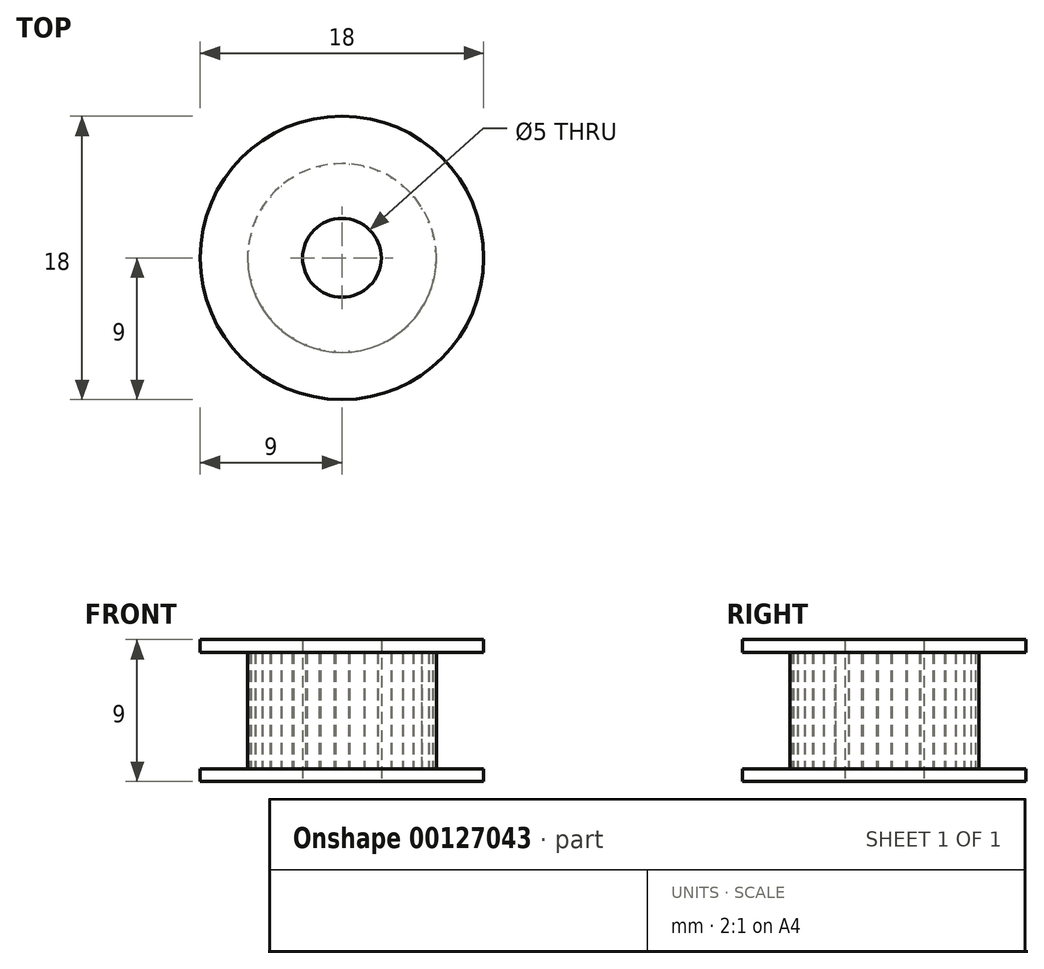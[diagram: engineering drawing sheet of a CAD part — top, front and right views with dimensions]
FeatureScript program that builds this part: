
annotation { "Feature Type Name" : "Feature", "Feature Type Description" : "" }
export const myFeature = defineFeature(function(context is Context, id is Id, definition is map)
    precondition{}
    {
        {
            var Q0;
            Q0=qCreatedBy(makeId("Top.planeOp"),FACE);
            var sketch = newSketch(context, id + "F0", { "sketchPlane" : qUnion([Q0])});
            skLineSegment(sketch, "E0", {"start": v(-19.17, 17.78) * mm, "end": v(-18.17, 17.78) * mm});
            skLineSegment(sketch, "E1", {"start": v(-18.17, 17.78) * mm, "end": v(-18.17, 18.4) * mm});
            skArc(sketch, "E2", {"start": v(-18.67, 18.85) * mm, "mid": v(-18.88, 19.07) * mm, "end": v(-19.17, 19.16) * mm});
            skArc(sketch, "E3", {"start": v(-18.58, 18.54) * mm, "mid": v(-18.61, 18.7) * mm, "end": v(-18.67, 18.85) * mm});
            skArc(sketch, "E4", {"start": v(-18.58, 18.54) * mm, "mid": v(-18.53, 18.44) * mm, "end": v(-18.43, 18.4) * mm});
            skLineSegment(sketch, "E5", {"start": v(-18.43, 18.4) * mm, "end": v(-18.17, 18.4) * mm});
            skArc(sketch, "E6.0.MirrorCS", {"start": v(-19.67, 18.85) * mm, "mid": v(-19.47, 19.07) * mm, "end": v(-19.17, 19.16) * mm});
            skArc(sketch, "E7.0.MirrorCS", {"start": v(-19.76, 18.54) * mm, "mid": v(-19.73, 18.7) * mm, "end": v(-19.67, 18.85) * mm});
            skArc(sketch, "E8.0.MirrorCS", {"start": v(-19.76, 18.54) * mm, "mid": v(-19.81, 18.44) * mm, "end": v(-19.91, 18.4) * mm});
            skLineSegment(sketch, "E9.0.MirrorCS", {"start": v(-19.91, 18.4) * mm, "end": v(-20.17, 18.4) * mm});
            skLineSegment(sketch, "E10.0.MirrorCS", {"start": v(-20.17, 17.78) * mm, "end": v(-20.17, 18.4) * mm});
            skLineSegment(sketch, "E11.0.MirrorCS", {"start": v(-19.17, 17.78) * mm, "end": v(-20.17, 17.78) * mm});
            skLineSegment(sketch, "E12.direction1", {"start": v(-20.17, 17.78) * mm, "end": v(-18.17, 17.78) * mm, "construction": true});
            skLineSegment(sketch, "E13", {"start": v(-20.17, 18.15) * mm, "end": v(-18.17, 18.15) * mm, "construction": true});
            skPoint(sketch, "E14", {"position": v(0, -5.25) * mm});
            skArc(sketch, "E15", {"start": v(0.38, -5.76) * mm, "mid": v(0, -5.25) * mm, "end": v(-0.38, -5.76) * mm});
            skArc(sketch, "E16", {"start": v(-0.38, -5.76) * mm, "mid": v(-0.38, -5.76) * mm, "end": v(-0.38, -5.77) * mm});
            skArc(sketch, "E17", {"start": v(0.38, -5.77) * mm, "mid": v(0.38, -5.76) * mm, "end": v(0.38, -5.76) * mm});
            skArc(sketch, "E18", {"start": v(0.4, -5.94) * mm, "mid": v(0.93, -5.88) * mm, "end": v(1.45, -5.77) * mm});
            skArc(sketch, "E19", {"start": v(0.38, -5.77) * mm, "mid": v(0.36, -5.9) * mm, "end": v(0.5, -5.93) * mm});
            skArc(sketch, "E20", {"start": v(-0.38, -5.77) * mm, "mid": v(-0.36, -5.9) * mm, "end": v(-0.5, -5.93) * mm});
            skArc(sketch, "E21.1.0", {"start": v(2.14, -5.36) * mm, "mid": v(1.62, -5) * mm, "end": v(1.42, -5.6) * mm});
            skPoint(sketch, "E21.1.1", {"position": v(1.62, -5) * mm});
            skArc(sketch, "E21.1.2", {"start": v(1.42, -5.6) * mm, "mid": v(1.42, -5.6) * mm, "end": v(1.42, -5.6) * mm});
            skArc(sketch, "E21.1.3", {"start": v(2.14, -5.37) * mm, "mid": v(2.17, -5.5) * mm, "end": v(2.3, -5.49) * mm});
            skArc(sketch, "E21.1.4", {"start": v(1.42, -5.6) * mm, "mid": v(1.48, -5.72) * mm, "end": v(1.36, -5.8) * mm});
            skArc(sketch, "E21.1.5", {"start": v(2.14, -5.37) * mm, "mid": v(2.14, -5.37) * mm, "end": v(2.14, -5.36) * mm});
            skArc(sketch, "E22.3.2.0", {"start": v(3.7, -4.44) * mm, "mid": v(3.08, -4.25) * mm, "end": v(3.08, -4.9) * mm});
            skPoint(sketch, "E22.4.2.0", {"position": v(3.08, -4.25) * mm});
            skArc(sketch, "E22.5.2.0", {"start": v(3.08, -4.9) * mm, "mid": v(3.08, -4.9) * mm, "end": v(3.08, -4.9) * mm});
            skArc(sketch, "E22.9.2.0", {"start": v(3.7, -4.44) * mm, "mid": v(3.76, -4.56) * mm, "end": v(3.88, -4.5) * mm});
            skArc(sketch, "E22.13.2.0", {"start": v(3.08, -4.9) * mm, "mid": v(3.17, -4.99) * mm, "end": v(3.08, -5.09) * mm});
            skArc(sketch, "E22.17.2.0", {"start": v(3.7, -4.44) * mm, "mid": v(3.7, -4.44) * mm, "end": v(3.7, -4.44) * mm});
            skArc(sketch, "E22.3.3.0", {"start": v(4.89, -3.08) * mm, "mid": v(4.25, -3.09) * mm, "end": v(4.43, -3.7) * mm});
            skPoint(sketch, "E22.4.3.0", {"position": v(4.25, -3.09) * mm});
            skArc(sketch, "E22.5.3.0", {"start": v(4.43, -3.7) * mm, "mid": v(4.44, -3.7) * mm, "end": v(4.44, -3.7) * mm});
            skArc(sketch, "E22.9.3.0", {"start": v(4.89, -3.08) * mm, "mid": v(4.98, -3.18) * mm, "end": v(5.09, -3.09) * mm});
            skArc(sketch, "E22.13.3.0", {"start": v(4.44, -3.7) * mm, "mid": v(4.56, -3.76) * mm, "end": v(4.5, -3.89) * mm});
            skArc(sketch, "E22.17.3.0", {"start": v(4.89, -3.08) * mm, "mid": v(4.89, -3.08) * mm, "end": v(4.89, -3.08) * mm});
            skArc(sketch, "E22.3.4.0", {"start": v(5.6, -1.42) * mm, "mid": v(5, -1.63) * mm, "end": v(5.36, -2.15) * mm});
            skPoint(sketch, "E22.4.4.0", {"position": v(5, -1.63) * mm});
            skArc(sketch, "E22.5.4.0", {"start": v(5.36, -2.15) * mm, "mid": v(5.36, -2.15) * mm, "end": v(5.36, -2.15) * mm});
            skArc(sketch, "E22.9.4.0", {"start": v(5.6, -1.42) * mm, "mid": v(5.72, -1.48) * mm, "end": v(5.79, -1.37) * mm});
            skArc(sketch, "E22.13.4.0", {"start": v(5.36, -2.15) * mm, "mid": v(5.5, -2.17) * mm, "end": v(5.48, -2.3) * mm});
            skArc(sketch, "E22.17.4.0", {"start": v(5.6, -1.42) * mm, "mid": v(5.6, -1.42) * mm, "end": v(5.6, -1.42) * mm});
            skArc(sketch, "E22.3.5.0", {"start": v(5.76, 0.38) * mm, "mid": v(5.25, 0) * mm, "end": v(5.76, -0.39) * mm});
            skPoint(sketch, "E22.4.5.0", {"position": v(5.25, 0) * mm});
            skArc(sketch, "E22.5.5.0", {"start": v(5.76, -0.39) * mm, "mid": v(5.76, -0.39) * mm, "end": v(5.76, -0.39) * mm});
            skArc(sketch, "E22.9.5.0", {"start": v(5.76, 0.37) * mm, "mid": v(5.9, 0.36) * mm, "end": v(5.93, 0.49) * mm});
            skArc(sketch, "E22.13.5.0", {"start": v(5.76, -0.39) * mm, "mid": v(5.9, -0.37) * mm, "end": v(5.93, -0.5) * mm});
            skArc(sketch, "E22.17.5.0", {"start": v(5.76, 0.37) * mm, "mid": v(5.76, 0.38) * mm, "end": v(5.76, 0.38) * mm});
            skArc(sketch, "E22.3.6.0", {"start": v(5.36, 2.14) * mm, "mid": v(5, 1.61) * mm, "end": v(5.6, 1.4) * mm});
            skPoint(sketch, "E22.4.6.0", {"position": v(5, 1.61) * mm});
            skArc(sketch, "E22.5.6.0", {"start": v(5.6, 1.4) * mm, "mid": v(5.6, 1.41) * mm, "end": v(5.6, 1.41) * mm});
            skArc(sketch, "E22.9.6.0", {"start": v(5.37, 2.14) * mm, "mid": v(5.5, 2.16) * mm, "end": v(5.49, 2.3) * mm});
            skArc(sketch, "E22.13.6.0", {"start": v(5.6, 1.41) * mm, "mid": v(5.72, 1.47) * mm, "end": v(5.8, 1.35) * mm});
            skArc(sketch, "E22.17.6.0", {"start": v(5.37, 2.14) * mm, "mid": v(5.36, 2.14) * mm, "end": v(5.36, 2.14) * mm});
            skArc(sketch, "E22.3.7.0", {"start": v(4.44, 3.69) * mm, "mid": v(4.25, 3.08) * mm, "end": v(4.89, 3.07) * mm});
            skPoint(sketch, "E22.4.7.0", {"position": v(4.25, 3.08) * mm});
            skArc(sketch, "E22.5.7.0", {"start": v(4.89, 3.07) * mm, "mid": v(4.89, 3.07) * mm, "end": v(4.89, 3.07) * mm});
            skArc(sketch, "E22.9.7.0", {"start": v(4.44, 3.69) * mm, "mid": v(4.56, 3.75) * mm, "end": v(4.5, 3.88) * mm});
            skArc(sketch, "E22.13.7.0", {"start": v(4.89, 3.07) * mm, "mid": v(4.99, 3.17) * mm, "end": v(5.09, 3.08) * mm});
            skArc(sketch, "E22.17.7.0", {"start": v(4.44, 3.69) * mm, "mid": v(4.44, 3.69) * mm, "end": v(4.44, 3.69) * mm});
            skArc(sketch, "E22.3.8.0", {"start": v(3.08, 4.88) * mm, "mid": v(3.09, 4.24) * mm, "end": v(3.7, 4.43) * mm});
            skPoint(sketch, "E22.4.8.0", {"position": v(3.09, 4.24) * mm});
            skArc(sketch, "E22.5.8.0", {"start": v(3.7, 4.43) * mm, "mid": v(3.7, 4.43) * mm, "end": v(3.7, 4.43) * mm});
            skArc(sketch, "E22.9.8.0", {"start": v(3.08, 4.88) * mm, "mid": v(3.18, 4.98) * mm, "end": v(3.09, 5.08) * mm});
            skArc(sketch, "E22.13.8.0", {"start": v(3.7, 4.43) * mm, "mid": v(3.76, 4.55) * mm, "end": v(3.89, 4.5) * mm});
            skArc(sketch, "E22.17.8.0", {"start": v(3.08, 4.88) * mm, "mid": v(3.08, 4.88) * mm, "end": v(3.08, 4.88) * mm});
            skArc(sketch, "E22.3.9.0", {"start": v(1.42, 5.6) * mm, "mid": v(1.63, 4.98) * mm, "end": v(2.15, 5.35) * mm});
            skPoint(sketch, "E22.4.9.0", {"position": v(1.63, 4.98) * mm});
            skArc(sketch, "E22.5.9.0", {"start": v(2.15, 5.35) * mm, "mid": v(2.15, 5.36) * mm, "end": v(2.15, 5.36) * mm});
            skArc(sketch, "E22.9.9.0", {"start": v(1.42, 5.6) * mm, "mid": v(1.48, 5.71) * mm, "end": v(1.37, 5.78) * mm});
            skArc(sketch, "E22.13.9.0", {"start": v(2.15, 5.36) * mm, "mid": v(2.17, 5.5) * mm, "end": v(2.3, 5.48) * mm});
            skArc(sketch, "E22.17.9.0", {"start": v(1.42, 5.6) * mm, "mid": v(1.42, 5.6) * mm, "end": v(1.42, 5.6) * mm});
            skArc(sketch, "E22.3.10.0", {"start": v(-0.38, 5.76) * mm, "mid": v(0, 5.24) * mm, "end": v(0.39, 5.76) * mm});
            skPoint(sketch, "E22.4.10.0", {"position": v(0, 5.24) * mm});
            skArc(sketch, "E22.5.10.0", {"start": v(0.39, 5.76) * mm, "mid": v(0.39, 5.76) * mm, "end": v(0.39, 5.76) * mm});
            skArc(sketch, "E22.9.10.0", {"start": v(-0.38, 5.76) * mm, "mid": v(-0.36, 5.9) * mm, "end": v(-0.49, 5.92) * mm});
            skArc(sketch, "E22.13.10.0", {"start": v(0.39, 5.76) * mm, "mid": v(0.37, 5.9) * mm, "end": v(0.5, 5.92) * mm});
            skArc(sketch, "E22.17.10.0", {"start": v(-0.38, 5.76) * mm, "mid": v(-0.38, 5.76) * mm, "end": v(-0.38, 5.76) * mm});
            skArc(sketch, "E22.3.11.0", {"start": v(-2.14, 5.36) * mm, "mid": v(-1.62, 4.99) * mm, "end": v(-1.41, 5.6) * mm});
            skPoint(sketch, "E22.4.11.0", {"position": v(-1.62, 4.99) * mm});
            skArc(sketch, "E22.5.11.0", {"start": v(-1.41, 5.6) * mm, "mid": v(-1.41, 5.6) * mm, "end": v(-1.41, 5.6) * mm});
            skArc(sketch, "E22.9.11.0", {"start": v(-2.14, 5.36) * mm, "mid": v(-2.16, 5.5) * mm, "end": v(-2.3, 5.48) * mm});
            skArc(sketch, "E22.13.11.0", {"start": v(-1.41, 5.6) * mm, "mid": v(-1.47, 5.72) * mm, "end": v(-1.36, 5.79) * mm});
            skArc(sketch, "E22.17.11.0", {"start": v(-2.14, 5.36) * mm, "mid": v(-2.14, 5.36) * mm, "end": v(-2.14, 5.36) * mm});
            skArc(sketch, "E22.3.12.0", {"start": v(-3.7, 4.43) * mm, "mid": v(-3.08, 4.24) * mm, "end": v(-3.07, 4.88) * mm});
            skPoint(sketch, "E22.4.12.0", {"position": v(-3.08, 4.24) * mm});
            skArc(sketch, "E22.5.12.0", {"start": v(-3.07, 4.88) * mm, "mid": v(-3.07, 4.88) * mm, "end": v(-3.07, 4.88) * mm});
            skArc(sketch, "E22.9.12.0", {"start": v(-3.7, 4.44) * mm, "mid": v(-3.75, 4.55) * mm, "end": v(-3.88, 4.5) * mm});
            skArc(sketch, "E22.13.12.0", {"start": v(-3.07, 4.88) * mm, "mid": v(-3.17, 4.98) * mm, "end": v(-3.08, 5.08) * mm});
            skArc(sketch, "E22.17.12.0", {"start": v(-3.7, 4.44) * mm, "mid": v(-3.7, 4.43) * mm, "end": v(-3.7, 4.43) * mm});
            skArc(sketch, "E22.3.13.0", {"start": v(-4.88, 3.07) * mm, "mid": v(-4.24, 3.08) * mm, "end": v(-4.43, 3.7) * mm});
            skPoint(sketch, "E22.4.13.0", {"position": v(-4.24, 3.08) * mm});
            skArc(sketch, "E22.5.13.0", {"start": v(-4.43, 3.7) * mm, "mid": v(-4.43, 3.7) * mm, "end": v(-4.43, 3.7) * mm});
            skArc(sketch, "E22.9.13.0", {"start": v(-4.88, 3.08) * mm, "mid": v(-4.98, 3.17) * mm, "end": v(-5.08, 3.08) * mm});
            skArc(sketch, "E22.13.13.0", {"start": v(-4.43, 3.7) * mm, "mid": v(-4.55, 3.76) * mm, "end": v(-4.5, 3.88) * mm});
            skArc(sketch, "E22.17.13.0", {"start": v(-4.88, 3.08) * mm, "mid": v(-4.88, 3.07) * mm, "end": v(-4.88, 3.07) * mm});
            skArc(sketch, "E22.3.14.0", {"start": v(-5.6, 1.41) * mm, "mid": v(-4.99, 1.62) * mm, "end": v(-5.36, 2.14) * mm});
            skPoint(sketch, "E22.4.14.0", {"position": v(-4.99, 1.62) * mm});
            skArc(sketch, "E22.5.14.0", {"start": v(-5.36, 2.14) * mm, "mid": v(-5.36, 2.14) * mm, "end": v(-5.36, 2.14) * mm});
            skArc(sketch, "E22.9.14.0", {"start": v(-5.6, 1.42) * mm, "mid": v(-5.72, 1.48) * mm, "end": v(-5.79, 1.36) * mm});
            skArc(sketch, "E22.13.14.0", {"start": v(-5.36, 2.14) * mm, "mid": v(-5.5, 2.17) * mm, "end": v(-5.48, 2.3) * mm});
            skArc(sketch, "E22.17.14.0", {"start": v(-5.6, 1.42) * mm, "mid": v(-5.6, 1.42) * mm, "end": v(-5.6, 1.41) * mm});
            skArc(sketch, "E22.3.15.0", {"start": v(-5.76, -0.39) * mm, "mid": v(-5.24, 0) * mm, "end": v(-5.76, 0.38) * mm});
            skPoint(sketch, "E22.4.15.0", {"position": v(-5.24, 0) * mm});
            skArc(sketch, "E22.5.15.0", {"start": v(-5.76, 0.38) * mm, "mid": v(-5.76, 0.38) * mm, "end": v(-5.76, 0.38) * mm});
            skArc(sketch, "E22.9.15.0", {"start": v(-5.76, -0.38) * mm, "mid": v(-5.9, -0.36) * mm, "end": v(-5.92, -0.5) * mm});
            skArc(sketch, "E22.13.15.0", {"start": v(-5.76, 0.38) * mm, "mid": v(-5.9, 0.36) * mm, "end": v(-5.92, 0.5) * mm});
            skArc(sketch, "E22.17.15.0", {"start": v(-5.76, -0.38) * mm, "mid": v(-5.76, -0.38) * mm, "end": v(-5.76, -0.39) * mm});
            skArc(sketch, "E22.3.16.0", {"start": v(-5.36, -2.15) * mm, "mid": v(-4.99, -1.62) * mm, "end": v(-5.6, -1.42) * mm});
            skPoint(sketch, "E22.4.16.0", {"position": v(-4.99, -1.62) * mm});
            skArc(sketch, "E22.5.16.0", {"start": v(-5.6, -1.42) * mm, "mid": v(-5.6, -1.42) * mm, "end": v(-5.6, -1.42) * mm});
            skArc(sketch, "E22.9.16.0", {"start": v(-5.36, -2.14) * mm, "mid": v(-5.5, -2.17) * mm, "end": v(-5.48, -2.3) * mm});
            skArc(sketch, "E22.13.16.0", {"start": v(-5.6, -1.42) * mm, "mid": v(-5.72, -1.48) * mm, "end": v(-5.79, -1.36) * mm});
            skArc(sketch, "E22.17.16.0", {"start": v(-5.36, -2.14) * mm, "mid": v(-5.36, -2.15) * mm, "end": v(-5.36, -2.15) * mm});
            skArc(sketch, "E22.3.17.0", {"start": v(-4.43, -3.7) * mm, "mid": v(-4.24, -3.09) * mm, "end": v(-4.88, -3.08) * mm});
            skPoint(sketch, "E22.4.17.0", {"position": v(-4.24, -3.09) * mm});
            skArc(sketch, "E22.5.17.0", {"start": v(-4.88, -3.08) * mm, "mid": v(-4.88, -3.08) * mm, "end": v(-4.88, -3.08) * mm});
            skArc(sketch, "E22.9.17.0", {"start": v(-4.44, -3.7) * mm, "mid": v(-4.56, -3.76) * mm, "end": v(-4.5, -3.88) * mm});
            skArc(sketch, "E22.13.17.0", {"start": v(-4.88, -3.08) * mm, "mid": v(-4.98, -3.17) * mm, "end": v(-5.08, -3.09) * mm});
            skArc(sketch, "E22.17.17.0", {"start": v(-4.44, -3.7) * mm, "mid": v(-4.43, -3.7) * mm, "end": v(-4.43, -3.7) * mm});
            skArc(sketch, "E22.3.18.0", {"start": v(-3.07, -4.89) * mm, "mid": v(-3.08, -4.25) * mm, "end": v(-3.7, -4.44) * mm});
            skPoint(sketch, "E22.4.18.0", {"position": v(-3.08, -4.25) * mm});
            skArc(sketch, "E22.5.18.0", {"start": v(-3.7, -4.44) * mm, "mid": v(-3.7, -4.44) * mm, "end": v(-3.7, -4.44) * mm});
            skArc(sketch, "E22.9.18.0", {"start": v(-3.08, -4.89) * mm, "mid": v(-3.17, -4.99) * mm, "end": v(-3.08, -5.09) * mm});
            skArc(sketch, "E22.13.18.0", {"start": v(-3.7, -4.44) * mm, "mid": v(-3.76, -4.56) * mm, "end": v(-3.88, -4.5) * mm});
            skArc(sketch, "E22.17.18.0", {"start": v(-3.08, -4.89) * mm, "mid": v(-3.08, -4.89) * mm, "end": v(-3.07, -4.89) * mm});
            skArc(sketch, "E22.3.19.0", {"start": v(-1.41, -5.6) * mm, "mid": v(-1.62, -5) * mm, "end": v(-2.14, -5.36) * mm});
            skPoint(sketch, "E22.4.19.0", {"position": v(-1.62, -5) * mm});
            skArc(sketch, "E22.5.19.0", {"start": v(-2.14, -5.36) * mm, "mid": v(-2.14, -5.36) * mm, "end": v(-2.14, -5.37) * mm});
            skArc(sketch, "E22.9.19.0", {"start": v(-1.42, -5.6) * mm, "mid": v(-1.48, -5.72) * mm, "end": v(-1.36, -5.8) * mm});
            skArc(sketch, "E22.13.19.0", {"start": v(-2.14, -5.37) * mm, "mid": v(-2.17, -5.5) * mm, "end": v(-2.3, -5.49) * mm});
            skArc(sketch, "E22.17.19.0", {"start": v(-1.42, -5.6) * mm, "mid": v(-1.42, -5.6) * mm, "end": v(-1.41, -5.6) * mm});
            skArc(sketch, "E23.trimOffspring", {"start": v(2.22, -5.52) * mm, "mid": v(2.7, -5.3) * mm, "end": v(3.16, -5.04) * mm});
            skArc(sketch, "E24.trimOffspring", {"start": v(3.82, -4.56) * mm, "mid": v(4.2, -4.2) * mm, "end": v(4.56, -3.82) * mm});
            skArc(sketch, "E25.trimOffspring", {"start": v(5.04, -3.16) * mm, "mid": v(5.28, -2.74) * mm, "end": v(5.48, -2.3) * mm});
            skArc(sketch, "E26.trimOffspring", {"start": v(5.77, -1.45) * mm, "mid": v(5.88, -0.94) * mm, "end": v(5.94, -0.42) * mm});
            skArc(sketch, "E27.trimOffspring", {"start": v(5.52, 2.23) * mm, "mid": v(5.3, 2.7) * mm, "end": v(5.05, 3.14) * mm});
            skArc(sketch, "E28.trimOffspring", {"start": v(4.56, 3.82) * mm, "mid": v(4.21, 4.2) * mm, "end": v(3.84, 4.55) * mm});
            skArc(sketch, "E29.trimOffspring", {"start": v(5.94, 0.4) * mm, "mid": v(5.88, 0.92) * mm, "end": v(5.77, 1.43) * mm});
            skArc(sketch, "E30.trimOffspring", {"start": v(3.15, 5.05) * mm, "mid": v(2.7, 5.3) * mm, "end": v(2.25, 5.5) * mm});
            skArc(sketch, "E31.trimOffspring", {"start": v(1.43, 5.78) * mm, "mid": v(0.94, 5.88) * mm, "end": v(0.44, 5.93) * mm});
            skArc(sketch, "E32.trimOffspring", {"start": v(-0.43, 5.93) * mm, "mid": v(-0.93, 5.88) * mm, "end": v(-1.41, 5.78) * mm});
            skArc(sketch, "E33.trimOffspring", {"start": v(-2.27, 5.5) * mm, "mid": v(-2.71, 5.3) * mm, "end": v(-3.13, 5.06) * mm});
            skArc(sketch, "E34.trimOffspring", {"start": v(-3.84, 4.54) * mm, "mid": v(-4.2, 4.2) * mm, "end": v(-4.54, 3.84) * mm});
            skArc(sketch, "E35.trimOffspring", {"start": v(-5.06, 3.13) * mm, "mid": v(-5.3, 2.7) * mm, "end": v(-5.51, 2.24) * mm});
            skArc(sketch, "E36.trimOffspring", {"start": v(-5.78, 1.42) * mm, "mid": v(-5.88, 0.93) * mm, "end": v(-5.93, 0.43) * mm});
            skArc(sketch, "E37.trimOffspring", {"start": v(-5.93, -0.48) * mm, "mid": v(-5.87, -0.96) * mm, "end": v(-5.77, -1.43) * mm});
            skArc(sketch, "E38.trimOffspring", {"start": v(-5.51, -2.24) * mm, "mid": v(-5.3, -2.7) * mm, "end": v(-5.05, -3.15) * mm});
            skArc(sketch, "E39.trimOffspring", {"start": v(-4.55, -3.83) * mm, "mid": v(-4.2, -4.2) * mm, "end": v(-3.82, -4.56) * mm});
            skArc(sketch, "E40.trimOffspring", {"start": v(-3.15, -5.05) * mm, "mid": v(-2.7, -5.3) * mm, "end": v(-2.22, -5.52) * mm});
            skArc(sketch, "E41.trimOffspring", {"start": v(-1.44, -5.77) * mm, "mid": v(-0.93, -5.88) * mm, "end": v(-0.4, -5.94) * mm});
            skCircle(sketch, "E42", {"center": v(0, 0) * mm, "radius": 6 * mm});
            skSolve(sketch);
        }
        {
            var Q0;
            Q0=makeQuery(id+"F0.imprint","IMPRINT",FACE,{"disambiguationData":[TD([[makeQuery(id+"F0.imprint","IMPRINT",EDGE,{"derivedFrom":sQuery(id+"F0.wireOp",EDGE,"E15")}),-1.0]])]});
            var Q1;
            Q1=makeQuery(id+"F0.imprint","IMPRINT",FACE,{"disambiguationData":[TD([[makeQuery(id+"F0.imprint","IMPRINT",EDGE,{"derivedFrom":sQuery(id+"F0.wireOp",EDGE,"E15")}),1.0]])]});
            extrude(context, id + "F1", {"entities" : qUnion([Q0, Q1]), "depth" : 7.4 * mm});
        }
        {
            var Q0;
            Q0=makeQuery(id+"F1.opExtrude","CAP_FACE",FACE,{"disambiguationData":[OSD([sQuery(id+"F0.wireOp",EDGE,"E15"),sQuery(id+"F0.wireOp",EDGE,"E16"),sQuery(id+"F0.wireOp",EDGE,"E17"),sQuery(id+"F0.wireOp",EDGE,"E18"),sQuery(id+"F0.wireOp",EDGE,"E19"),sQuery(id+"F0.wireOp",EDGE,"E20"),sQuery(id+"F0.wireOp",EDGE,"E21.1.0"),sQuery(id+"F0.wireOp",EDGE,"E21.1.2"),sQuery(id+"F0.wireOp",EDGE,"E21.1.3"),sQuery(id+"F0.wireOp",EDGE,"E21.1.4"),sQuery(id+"F0.wireOp",EDGE,"E21.1.5"),sQuery(id+"F0.wireOp",EDGE,"E22.3.2.0"),sQuery(id+"F0.wireOp",EDGE,"E22.5.2.0"),sQuery(id+"F0.wireOp",EDGE,"E22.9.2.0"),sQuery(id+"F0.wireOp",EDGE,"E22.13.2.0"),sQuery(id+"F0.wireOp",EDGE,"E22.17.2.0"),sQuery(id+"F0.wireOp",EDGE,"E22.3.3.0"),sQuery(id+"F0.wireOp",EDGE,"E22.5.3.0"),sQuery(id+"F0.wireOp",EDGE,"E22.9.3.0"),sQuery(id+"F0.wireOp",EDGE,"E22.13.3.0"),sQuery(id+"F0.wireOp",EDGE,"E22.17.3.0"),sQuery(id+"F0.wireOp",EDGE,"E22.3.4.0"),sQuery(id+"F0.wireOp",EDGE,"E22.5.4.0"),sQuery(id+"F0.wireOp",EDGE,"E22.9.4.0"),sQuery(id+"F0.wireOp",EDGE,"E22.13.4.0"),sQuery(id+"F0.wireOp",EDGE,"E22.17.4.0"),sQuery(id+"F0.wireOp",EDGE,"E22.3.5.0"),sQuery(id+"F0.wireOp",EDGE,"E22.5.5.0"),sQuery(id+"F0.wireOp",EDGE,"E22.9.5.0"),sQuery(id+"F0.wireOp",EDGE,"E22.13.5.0"),sQuery(id+"F0.wireOp",EDGE,"E22.17.5.0"),sQuery(id+"F0.wireOp",EDGE,"E22.3.6.0"),sQuery(id+"F0.wireOp",EDGE,"E22.5.6.0"),sQuery(id+"F0.wireOp",EDGE,"E22.9.6.0"),sQuery(id+"F0.wireOp",EDGE,"E22.13.6.0"),sQuery(id+"F0.wireOp",EDGE,"E22.17.6.0"),sQuery(id+"F0.wireOp",EDGE,"E22.3.7.0"),sQuery(id+"F0.wireOp",EDGE,"E22.5.7.0"),sQuery(id+"F0.wireOp",EDGE,"E22.9.7.0"),sQuery(id+"F0.wireOp",EDGE,"E22.13.7.0"),sQuery(id+"F0.wireOp",EDGE,"E22.17.7.0"),sQuery(id+"F0.wireOp",EDGE,"E22.3.8.0"),sQuery(id+"F0.wireOp",EDGE,"E22.5.8.0"),sQuery(id+"F0.wireOp",EDGE,"E22.9.8.0"),sQuery(id+"F0.wireOp",EDGE,"E22.13.8.0"),sQuery(id+"F0.wireOp",EDGE,"E22.17.8.0"),sQuery(id+"F0.wireOp",EDGE,"E22.3.9.0"),sQuery(id+"F0.wireOp",EDGE,"E22.5.9.0"),sQuery(id+"F0.wireOp",EDGE,"E22.9.9.0"),sQuery(id+"F0.wireOp",EDGE,"E22.13.9.0"),sQuery(id+"F0.wireOp",EDGE,"E22.17.9.0"),sQuery(id+"F0.wireOp",EDGE,"E22.3.10.0"),sQuery(id+"F0.wireOp",EDGE,"E22.5.10.0"),sQuery(id+"F0.wireOp",EDGE,"E22.9.10.0"),sQuery(id+"F0.wireOp",EDGE,"E22.13.10.0"),sQuery(id+"F0.wireOp",EDGE,"E22.17.10.0"),sQuery(id+"F0.wireOp",EDGE,"E22.3.11.0"),sQuery(id+"F0.wireOp",EDGE,"E22.5.11.0"),sQuery(id+"F0.wireOp",EDGE,"E22.9.11.0"),sQuery(id+"F0.wireOp",EDGE,"E22.13.11.0"),sQuery(id+"F0.wireOp",EDGE,"E22.17.11.0"),sQuery(id+"F0.wireOp",EDGE,"E22.3.12.0"),sQuery(id+"F0.wireOp",EDGE,"E22.5.12.0"),sQuery(id+"F0.wireOp",EDGE,"E22.9.12.0"),sQuery(id+"F0.wireOp",EDGE,"E22.13.12.0"),sQuery(id+"F0.wireOp",EDGE,"E22.17.12.0"),sQuery(id+"F0.wireOp",EDGE,"E22.3.13.0"),sQuery(id+"F0.wireOp",EDGE,"E22.5.13.0"),sQuery(id+"F0.wireOp",EDGE,"E22.9.13.0"),sQuery(id+"F0.wireOp",EDGE,"E22.13.13.0"),sQuery(id+"F0.wireOp",EDGE,"E22.17.13.0"),sQuery(id+"F0.wireOp",EDGE,"E22.3.14.0"),sQuery(id+"F0.wireOp",EDGE,"E22.5.14.0"),sQuery(id+"F0.wireOp",EDGE,"E22.9.14.0"),sQuery(id+"F0.wireOp",EDGE,"E22.13.14.0"),sQuery(id+"F0.wireOp",EDGE,"E22.17.14.0"),sQuery(id+"F0.wireOp",EDGE,"E22.3.15.0"),sQuery(id+"F0.wireOp",EDGE,"E22.5.15.0"),sQuery(id+"F0.wireOp",EDGE,"E22.9.15.0"),sQuery(id+"F0.wireOp",EDGE,"E22.13.15.0"),sQuery(id+"F0.wireOp",EDGE,"E22.17.15.0"),sQuery(id+"F0.wireOp",EDGE,"E22.3.16.0"),sQuery(id+"F0.wireOp",EDGE,"E22.5.16.0"),sQuery(id+"F0.wireOp",EDGE,"E22.9.16.0"),sQuery(id+"F0.wireOp",EDGE,"E22.13.16.0"),sQuery(id+"F0.wireOp",EDGE,"E22.17.16.0"),sQuery(id+"F0.wireOp",EDGE,"E22.3.17.0"),sQuery(id+"F0.wireOp",EDGE,"E22.5.17.0"),sQuery(id+"F0.wireOp",EDGE,"E22.9.17.0"),sQuery(id+"F0.wireOp",EDGE,"E22.13.17.0"),sQuery(id+"F0.wireOp",EDGE,"E22.17.17.0"),sQuery(id+"F0.wireOp",EDGE,"E22.3.18.0"),sQuery(id+"F0.wireOp",EDGE,"E22.5.18.0"),sQuery(id+"F0.wireOp",EDGE,"E22.9.18.0"),sQuery(id+"F0.wireOp",EDGE,"E22.13.18.0"),sQuery(id+"F0.wireOp",EDGE,"E22.17.18.0"),sQuery(id+"F0.wireOp",EDGE,"E22.3.19.0"),sQuery(id+"F0.wireOp",EDGE,"E22.5.19.0"),sQuery(id+"F0.wireOp",EDGE,"E22.9.19.0"),sQuery(id+"F0.wireOp",EDGE,"E22.13.19.0"),sQuery(id+"F0.wireOp",EDGE,"E22.17.19.0"),sQuery(id+"F0.wireOp",EDGE,"E23.trimOffspring"),sQuery(id+"F0.wireOp",EDGE,"E24.trimOffspring"),sQuery(id+"F0.wireOp",EDGE,"E25.trimOffspring"),sQuery(id+"F0.wireOp",EDGE,"E26.trimOffspring"),sQuery(id+"F0.wireOp",EDGE,"E27.trimOffspring"),sQuery(id+"F0.wireOp",EDGE,"E28.trimOffspring"),sQuery(id+"F0.wireOp",EDGE,"E29.trimOffspring"),sQuery(id+"F0.wireOp",EDGE,"E30.trimOffspring"),sQuery(id+"F0.wireOp",EDGE,"E31.trimOffspring"),sQuery(id+"F0.wireOp",EDGE,"E32.trimOffspring"),sQuery(id+"F0.wireOp",EDGE,"E33.trimOffspring"),sQuery(id+"F0.wireOp",EDGE,"E34.trimOffspring"),sQuery(id+"F0.wireOp",EDGE,"E35.trimOffspring"),sQuery(id+"F0.wireOp",EDGE,"E36.trimOffspring"),sQuery(id+"F0.wireOp",EDGE,"E37.trimOffspring"),sQuery(id+"F0.wireOp",EDGE,"E38.trimOffspring"),sQuery(id+"F0.wireOp",EDGE,"E39.trimOffspring"),sQuery(id+"F0.wireOp",EDGE,"E40.trimOffspring"),sQuery(id+"F0.wireOp",EDGE,"E41.trimOffspring")])],"isStart":false});
            var sketch = newSketch(context, id + "F2", { "sketchPlane" : qUnion([Q0])});
            skCircle(sketch, "E43", {"center": v(0, 0) * mm, "radius": 9 * mm});
            skSolve(sketch);
        }
        {
            var Q0;
            Q0=qSketchRegion(id+"F2",true);
            extrude(context, id + "F3", {"entities" : qUnion([Q0]), "operationType" : NewBodyOperationType.ADD, "depth" : 0.8 * mm});
        }
        {
            var Q0;
            Q0=makeQuery(id+"F1.opExtrude","CAP_FACE",FACE,{"disambiguationData":[OSD([sQuery(id+"F0.wireOp",EDGE,"E15"),sQuery(id+"F0.wireOp",EDGE,"E16"),sQuery(id+"F0.wireOp",EDGE,"E17"),sQuery(id+"F0.wireOp",EDGE,"E18"),sQuery(id+"F0.wireOp",EDGE,"E19"),sQuery(id+"F0.wireOp",EDGE,"E20"),sQuery(id+"F0.wireOp",EDGE,"E21.1.0"),sQuery(id+"F0.wireOp",EDGE,"E21.1.2"),sQuery(id+"F0.wireOp",EDGE,"E21.1.3"),sQuery(id+"F0.wireOp",EDGE,"E21.1.4"),sQuery(id+"F0.wireOp",EDGE,"E21.1.5"),sQuery(id+"F0.wireOp",EDGE,"E22.3.2.0"),sQuery(id+"F0.wireOp",EDGE,"E22.5.2.0"),sQuery(id+"F0.wireOp",EDGE,"E22.9.2.0"),sQuery(id+"F0.wireOp",EDGE,"E22.13.2.0"),sQuery(id+"F0.wireOp",EDGE,"E22.17.2.0"),sQuery(id+"F0.wireOp",EDGE,"E22.3.3.0"),sQuery(id+"F0.wireOp",EDGE,"E22.5.3.0"),sQuery(id+"F0.wireOp",EDGE,"E22.9.3.0"),sQuery(id+"F0.wireOp",EDGE,"E22.13.3.0"),sQuery(id+"F0.wireOp",EDGE,"E22.17.3.0"),sQuery(id+"F0.wireOp",EDGE,"E22.3.4.0"),sQuery(id+"F0.wireOp",EDGE,"E22.5.4.0"),sQuery(id+"F0.wireOp",EDGE,"E22.9.4.0"),sQuery(id+"F0.wireOp",EDGE,"E22.13.4.0"),sQuery(id+"F0.wireOp",EDGE,"E22.17.4.0"),sQuery(id+"F0.wireOp",EDGE,"E22.3.5.0"),sQuery(id+"F0.wireOp",EDGE,"E22.5.5.0"),sQuery(id+"F0.wireOp",EDGE,"E22.9.5.0"),sQuery(id+"F0.wireOp",EDGE,"E22.13.5.0"),sQuery(id+"F0.wireOp",EDGE,"E22.17.5.0"),sQuery(id+"F0.wireOp",EDGE,"E22.3.6.0"),sQuery(id+"F0.wireOp",EDGE,"E22.5.6.0"),sQuery(id+"F0.wireOp",EDGE,"E22.9.6.0"),sQuery(id+"F0.wireOp",EDGE,"E22.13.6.0"),sQuery(id+"F0.wireOp",EDGE,"E22.17.6.0"),sQuery(id+"F0.wireOp",EDGE,"E22.3.7.0"),sQuery(id+"F0.wireOp",EDGE,"E22.5.7.0"),sQuery(id+"F0.wireOp",EDGE,"E22.9.7.0"),sQuery(id+"F0.wireOp",EDGE,"E22.13.7.0"),sQuery(id+"F0.wireOp",EDGE,"E22.17.7.0"),sQuery(id+"F0.wireOp",EDGE,"E22.3.8.0"),sQuery(id+"F0.wireOp",EDGE,"E22.5.8.0"),sQuery(id+"F0.wireOp",EDGE,"E22.9.8.0"),sQuery(id+"F0.wireOp",EDGE,"E22.13.8.0"),sQuery(id+"F0.wireOp",EDGE,"E22.17.8.0"),sQuery(id+"F0.wireOp",EDGE,"E22.3.9.0"),sQuery(id+"F0.wireOp",EDGE,"E22.5.9.0"),sQuery(id+"F0.wireOp",EDGE,"E22.9.9.0"),sQuery(id+"F0.wireOp",EDGE,"E22.13.9.0"),sQuery(id+"F0.wireOp",EDGE,"E22.17.9.0"),sQuery(id+"F0.wireOp",EDGE,"E22.3.10.0"),sQuery(id+"F0.wireOp",EDGE,"E22.5.10.0"),sQuery(id+"F0.wireOp",EDGE,"E22.9.10.0"),sQuery(id+"F0.wireOp",EDGE,"E22.13.10.0"),sQuery(id+"F0.wireOp",EDGE,"E22.17.10.0"),sQuery(id+"F0.wireOp",EDGE,"E22.3.11.0"),sQuery(id+"F0.wireOp",EDGE,"E22.5.11.0"),sQuery(id+"F0.wireOp",EDGE,"E22.9.11.0"),sQuery(id+"F0.wireOp",EDGE,"E22.13.11.0"),sQuery(id+"F0.wireOp",EDGE,"E22.17.11.0"),sQuery(id+"F0.wireOp",EDGE,"E22.3.12.0"),sQuery(id+"F0.wireOp",EDGE,"E22.5.12.0"),sQuery(id+"F0.wireOp",EDGE,"E22.9.12.0"),sQuery(id+"F0.wireOp",EDGE,"E22.13.12.0"),sQuery(id+"F0.wireOp",EDGE,"E22.17.12.0"),sQuery(id+"F0.wireOp",EDGE,"E22.3.13.0"),sQuery(id+"F0.wireOp",EDGE,"E22.5.13.0"),sQuery(id+"F0.wireOp",EDGE,"E22.9.13.0"),sQuery(id+"F0.wireOp",EDGE,"E22.13.13.0"),sQuery(id+"F0.wireOp",EDGE,"E22.17.13.0"),sQuery(id+"F0.wireOp",EDGE,"E22.3.14.0"),sQuery(id+"F0.wireOp",EDGE,"E22.5.14.0"),sQuery(id+"F0.wireOp",EDGE,"E22.9.14.0"),sQuery(id+"F0.wireOp",EDGE,"E22.13.14.0"),sQuery(id+"F0.wireOp",EDGE,"E22.17.14.0"),sQuery(id+"F0.wireOp",EDGE,"E22.3.15.0"),sQuery(id+"F0.wireOp",EDGE,"E22.5.15.0"),sQuery(id+"F0.wireOp",EDGE,"E22.9.15.0"),sQuery(id+"F0.wireOp",EDGE,"E22.13.15.0"),sQuery(id+"F0.wireOp",EDGE,"E22.17.15.0"),sQuery(id+"F0.wireOp",EDGE,"E22.3.16.0"),sQuery(id+"F0.wireOp",EDGE,"E22.5.16.0"),sQuery(id+"F0.wireOp",EDGE,"E22.9.16.0"),sQuery(id+"F0.wireOp",EDGE,"E22.13.16.0"),sQuery(id+"F0.wireOp",EDGE,"E22.17.16.0"),sQuery(id+"F0.wireOp",EDGE,"E22.3.17.0"),sQuery(id+"F0.wireOp",EDGE,"E22.5.17.0"),sQuery(id+"F0.wireOp",EDGE,"E22.9.17.0"),sQuery(id+"F0.wireOp",EDGE,"E22.13.17.0"),sQuery(id+"F0.wireOp",EDGE,"E22.17.17.0"),sQuery(id+"F0.wireOp",EDGE,"E22.3.18.0"),sQuery(id+"F0.wireOp",EDGE,"E22.5.18.0"),sQuery(id+"F0.wireOp",EDGE,"E22.9.18.0"),sQuery(id+"F0.wireOp",EDGE,"E22.13.18.0"),sQuery(id+"F0.wireOp",EDGE,"E22.17.18.0"),sQuery(id+"F0.wireOp",EDGE,"E22.3.19.0"),sQuery(id+"F0.wireOp",EDGE,"E22.5.19.0"),sQuery(id+"F0.wireOp",EDGE,"E22.9.19.0"),sQuery(id+"F0.wireOp",EDGE,"E22.13.19.0"),sQuery(id+"F0.wireOp",EDGE,"E22.17.19.0"),sQuery(id+"F0.wireOp",EDGE,"E23.trimOffspring"),sQuery(id+"F0.wireOp",EDGE,"E24.trimOffspring"),sQuery(id+"F0.wireOp",EDGE,"E25.trimOffspring"),sQuery(id+"F0.wireOp",EDGE,"E26.trimOffspring"),sQuery(id+"F0.wireOp",EDGE,"E27.trimOffspring"),sQuery(id+"F0.wireOp",EDGE,"E28.trimOffspring"),sQuery(id+"F0.wireOp",EDGE,"E29.trimOffspring"),sQuery(id+"F0.wireOp",EDGE,"E30.trimOffspring"),sQuery(id+"F0.wireOp",EDGE,"E31.trimOffspring"),sQuery(id+"F0.wireOp",EDGE,"E32.trimOffspring"),sQuery(id+"F0.wireOp",EDGE,"E33.trimOffspring"),sQuery(id+"F0.wireOp",EDGE,"E34.trimOffspring"),sQuery(id+"F0.wireOp",EDGE,"E35.trimOffspring"),sQuery(id+"F0.wireOp",EDGE,"E36.trimOffspring"),sQuery(id+"F0.wireOp",EDGE,"E37.trimOffspring"),sQuery(id+"F0.wireOp",EDGE,"E38.trimOffspring"),sQuery(id+"F0.wireOp",EDGE,"E39.trimOffspring"),sQuery(id+"F0.wireOp",EDGE,"E40.trimOffspring"),sQuery(id+"F0.wireOp",EDGE,"E41.trimOffspring")])],"isStart":true});
            var sketch = newSketch(context, id + "F4", { "sketchPlane" : qUnion([Q0])});
            skCircle(sketch, "E44", {"center": v(0, 0) * mm, "radius": 9 * mm});
            skSolve(sketch);
        }
        {
            var Q0;
            Q0=qSketchRegion(id+"F4",true);
            extrude(context, id + "F5", {"entities" : qUnion([Q0]), "operationType" : NewBodyOperationType.ADD, "depth" : 0.8 * mm});
        }
        {
            var Q0;
            Q0=makeQuery(id+"F5.opExtrude","CAP_FACE",FACE,{"disambiguationData":[OSD([sQuery(id+"F4.wireOp",EDGE,"E44")])],"isStart":false});
            var sketch = newSketch(context, id + "F6", { "sketchPlane" : qUnion([Q0])});
            skCircle(sketch, "E45", {"center": v(0, 0) * mm, "radius": 2.5 * mm});
            skSolve(sketch);
        }
        {
            var Q0;
            Q0=qSketchRegion(id+"F6",true);
            extrude(context, id + "F7", {"entities" : qUnion([Q0]), "operationType" : NewBodyOperationType.REMOVE, "endBound" : BoundingType.THROUGH_ALL, "oppositeDirection" : true, "depth" : 25 * mm});
        }
    });
